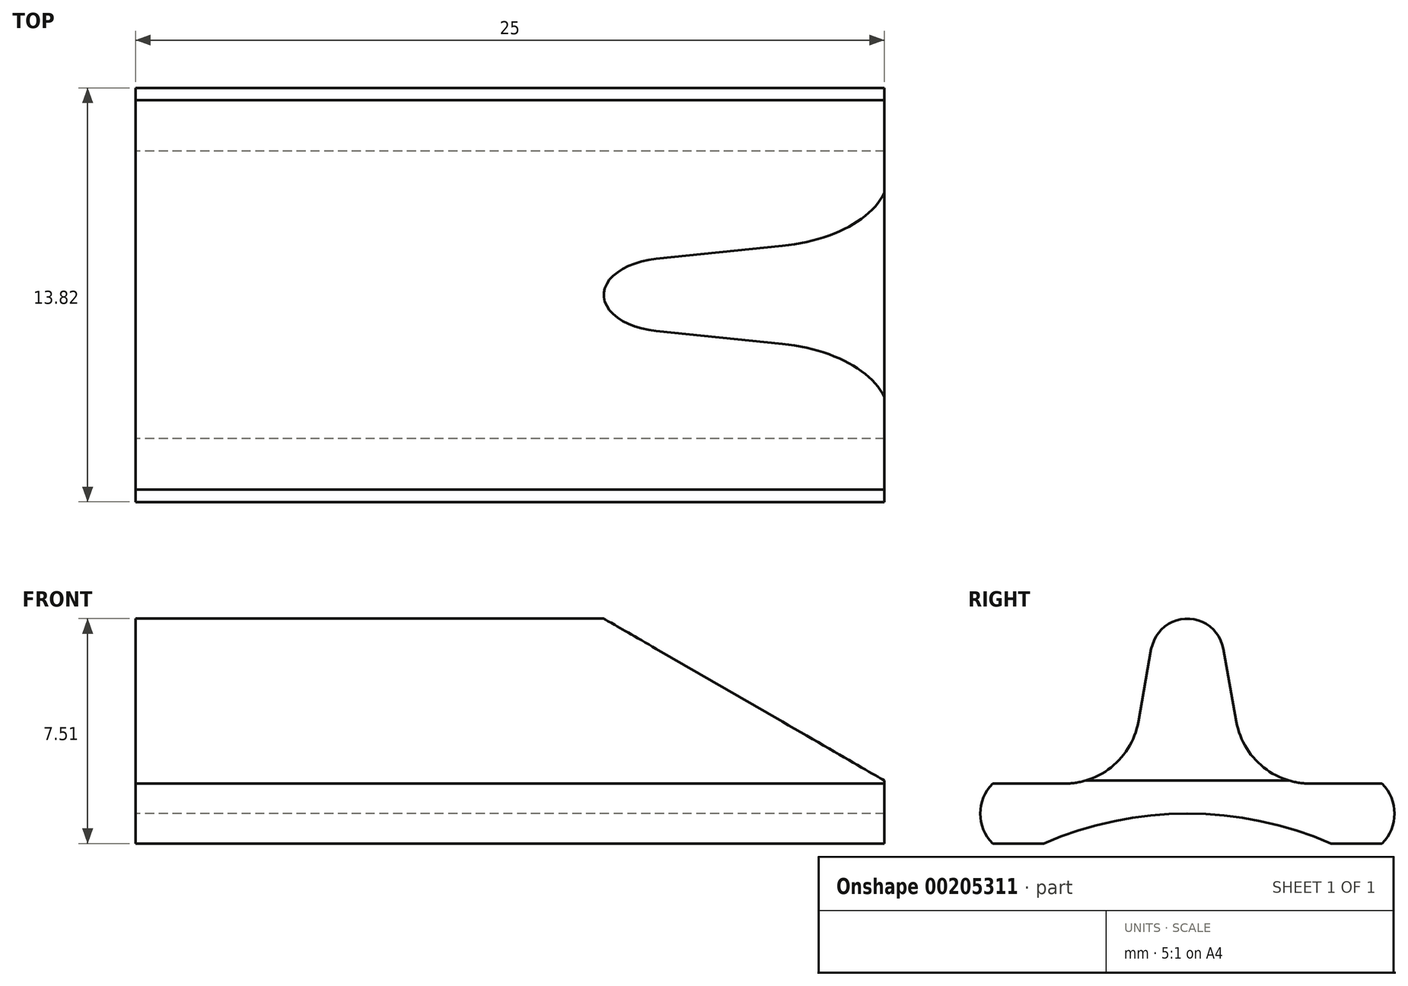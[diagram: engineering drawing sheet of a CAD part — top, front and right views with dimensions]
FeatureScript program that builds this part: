
annotation { "Feature Type Name" : "Feature", "Feature Type Description" : "" }
export const myFeature = defineFeature(function(context is Context, id is Id, definition is map)
    precondition{}
    {
        {
            var Q0;
            Q0=qCreatedBy(makeId("Right.planeOp"),FACE);
            var sketch = newSketch(context, id + "F0", { "sketchPlane" : qUnion([Q0])});
            skLineSegment(sketch, "E0", {"start": v(0, 0) * mm, "end": v(0, -11) * mm, "construction": true});
            skLineSegment(sketch, "E1", {"start": v(-4.8, 0) * mm, "end": v(-6.5, 0) * mm});
            skLineSegment(sketch, "E2", {"start": v(-2, 2) * mm, "end": v(-6.5, 2) * mm});
            skArc(sketch, "E3", {"start": v(-6.5, 2) * mm, "mid": v(-6.91, 1) * mm, "end": v(-6.5, 0) * mm});
            skLineSegment(sketch, "E4", {"start": v(-2, 2) * mm, "end": v(-1.2, 6.5) * mm});
            skArc(sketch, "E5", {"start": v(1.2, 6.5) * mm, "mid": v(0, 7.51) * mm, "end": v(-1.2, 6.5) * mm});
            skLineSegment(sketch, "E6", {"start": v(0, 6.29) * mm, "end": v(0, 0) * mm, "construction": true});
            skLineSegment(sketch, "E7", {"start": v(4.8, 0) * mm, "end": v(6.5, 0) * mm});
            skLineSegment(sketch, "E8", {"start": v(6.5, 2) * mm, "end": v(2, 2) * mm});
            skLineSegment(sketch, "E9", {"start": v(2, 2) * mm, "end": v(1.2, 6.5) * mm});
            skArc(sketch, "E10", {"start": v(6.5, 0) * mm, "mid": v(6.91, 1) * mm, "end": v(6.5, 2) * mm});
            skArc(sketch, "E11", {"start": v(-4.8, 0) * mm, "mid": v(0, -23) * mm, "end": v(4.8, 0) * mm, "construction": true});
            skArc(sketch, "E12", {"start": v(4.8, 0) * mm, "mid": v(0, 1) * mm, "end": v(-4.8, 0) * mm});
            skLineSegment(sketch, "E13", {"start": v(-6.5, 2) * mm, "end": v(-6.5, 0) * mm, "construction": true});
            skLineSegment(sketch, "E14", {"start": v(6.5, 2) * mm, "end": v(6.5, 0) * mm, "construction": true});
            skPoint(sketch, "E15", {"position": v(-6.5, 1) * mm});
            skSolve(sketch);
        }
        {
            var Q0;
            Q0=makeQuery(id+"F0.imprint","IMPRINT",FACE,{"disambiguationData":[TD([[makeQuery(id+"F0.imprint","IMPRINT",EDGE,{"derivedFrom":sQuery(id+"F0.wireOp",EDGE,"E1")}),-1.0]])]});
            extrude(context, id + "F1", {"entities" : qUnion([Q0]), "depth" : 25 * mm});
        }
        {
            var Q0;
            Q0=makeQuery(id+"F1.opExtrude","SWEPT_EDGE",EDGE,{"disambiguationData":[OSD([sQuery(id+"F0.wireOp",EDGE,"E8"),sQuery(id+"F0.wireOp",EDGE,"E9")])]});
            var Q1;
            Q1=makeQuery(id+"F1.opExtrude","SWEPT_EDGE",EDGE,{"disambiguationData":[OSD([sQuery(id+"F0.wireOp",EDGE,"E2"),sQuery(id+"F0.wireOp",EDGE,"E4")])]});
            fillet(context, id + "F2", {"entities" : qUnion([Q0, Q1]), "radius" : 2.5 * mm, "tangentPropagation" : true, "allowEdgeOverflow" : false});
        }
        {
            var Q0;
            Q0=qCreatedBy(makeId("Front.planeOp"),FACE);
            var sketch = newSketch(context, id + "F3", { "sketchPlane" : qUnion([Q0])});
            skLineSegment(sketch, "E16", {"start": v(30, -0.79) * mm, "end": v(8, 11.91) * mm});
            skLineSegment(sketch, "E17", {"start": v(8, 11.91) * mm, "end": v(30, 11.91) * mm});
            skLineSegment(sketch, "E18", {"start": v(30, 11.91) * mm, "end": v(30, -0.79) * mm});
            skSolve(sketch);
        }
        {
            var Q0;
            Q0=makeQuery(id+"F3.imprint","IMPRINT",FACE,{"disambiguationData":[TD([[makeQuery(id+"F3.imprint","IMPRINT",EDGE,{"derivedFrom":sQuery(id+"F3.wireOp",EDGE,"E16")}),-1.0]])]});
            extrude(context, id + "F4", {"entities" : qUnion([Q0]), "operationType" : NewBodyOperationType.REMOVE, "endBound" : BoundingType.THROUGH_ALL, "oppositeDirection" : true, "depth" : 25 * mm, "hasSecondDirection" : true, "secondDirectionBound" : SecondDirectionBoundingType.THROUGH_ALL, "secondDirectionOppositeDirection" : false, "secondDirectionDepth" : 25 * mm});
        }
    });
